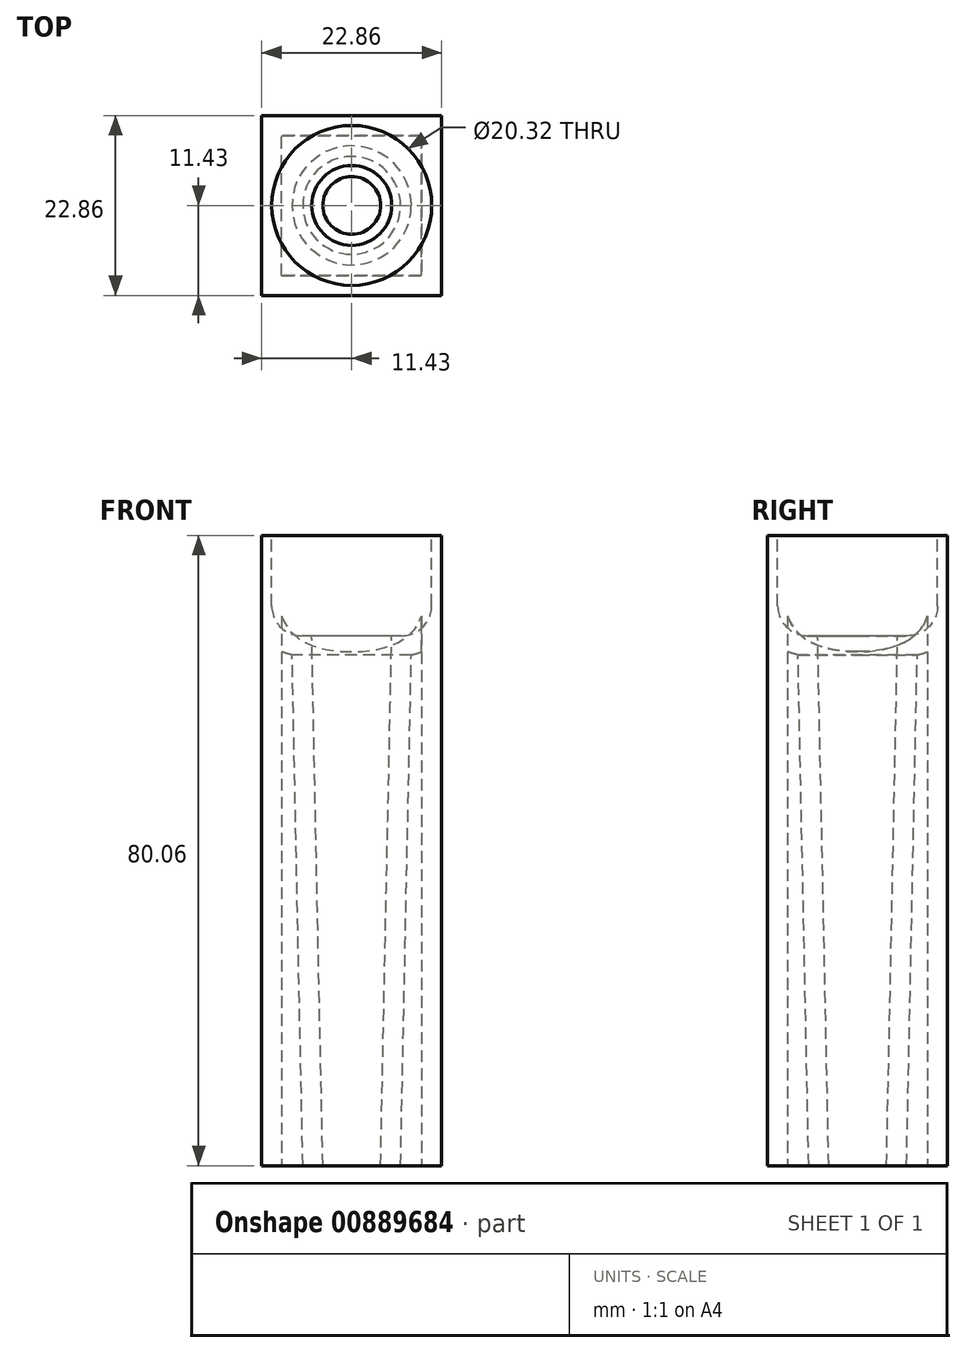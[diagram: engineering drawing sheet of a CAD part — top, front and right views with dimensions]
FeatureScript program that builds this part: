
annotation { "Feature Type Name" : "Feature", "Feature Type Description" : "" }
export const myFeature = defineFeature(function(context is Context, id is Id, definition is map)
    precondition{}
    {
        {
            var Q0;
            Q0=qCreatedBy(makeId("Top.planeOp"),FACE);
            var sketch = newSketch(context, id + "F0", { "sketchPlane" : qUnion([Q0])});
            skLineSegment(sketch, "E0.bottom", {"start": v(11.43, -11.43) * mm, "end": v(-11.43, -11.43) * mm});
            skLineSegment(sketch, "E0.top", {"start": v(11.43, 11.43) * mm, "end": v(-11.43, 11.43) * mm});
            skLineSegment(sketch, "E0.left", {"start": v(11.43, -11.43) * mm, "end": v(11.43, 11.43) * mm});
            skLineSegment(sketch, "E0.right", {"start": v(-11.43, -11.43) * mm, "end": v(-11.43, 11.43) * mm});
            skPoint(sketch, "E0.middle", {"position": v(0, 0) * mm});
            skSolve(sketch);
        }
        {
            var Q0;
            Q0 = qSketchRegion(id + "F0", true);
            extrude(context, id + "F1", {"entities" : qUnion([Q0]), "depth" : 67.3 * mm, "offsetDistance" : 25.4 * mm});
        }
        {
            var Q0;
            Q0=makeQuery(id+"F1.opExtrude","CAP_FACE",FACE,{"disambiguationData":[OSD([sQuery(id+"F0.wireOp",EDGE,"E0.bottom"),sQuery(id+"F0.wireOp",EDGE,"E0.top"),sQuery(id+"F0.wireOp",EDGE,"E0.left"),sQuery(id+"F0.wireOp",EDGE,"E0.right")])],"isStart":false});
            var sketch = newSketch(context, id + "F2", { "sketchPlane" : qUnion([Q0])});
            skLineSegment(sketch, "E1.bottom", {"start": v(11.43, -11.43) * mm, "end": v(-11.43, -11.43) * mm});
            skLineSegment(sketch, "E1.top", {"start": v(11.43, 11.43) * mm, "end": v(-11.43, 11.43) * mm});
            skLineSegment(sketch, "E1.left", {"start": v(11.43, -11.43) * mm, "end": v(11.43, 11.43) * mm});
            skLineSegment(sketch, "E1.right", {"start": v(-11.43, -11.43) * mm, "end": v(-11.43, 11.43) * mm});
            skPoint(sketch, "E1.middle", {"position": v(0, 0) * mm});
            skSolve(sketch);
        }
        {
            var Q0;
            Q0 = qSketchRegion(id + "F2", true);
            extrude(context, id + "F3", {"entities" : qUnion([Q0]), "operationType" : NewBodyOperationType.ADD, "depth" : 12.75 * mm, "offsetDistance" : 25.4 * mm});
        }
        {
            var Q0;
            Q0=qCreatedBy(makeId("Right.planeOp"),FACE);
            var sketch = newSketch(context, id + "F4", { "sketchPlane" : qUnion([Q0])});
            skLineSegment(sketch, "E2", {"start": v(0, 67.31) * mm, "end": v(-5.08, 67.31) * mm});
            skLineSegment(sketch, "E3", {"start": v(0, 67.31) * mm, "end": v(0, -11.43) * mm});
            skLineSegment(sketch, "E4", {"start": v(0, -11.43) * mm, "end": v(-3.43, -11.43) * mm});
            skLineSegment(sketch, "E5", {"start": v(-5.08, 67.31) * mm, "end": v(-3.43, -11.43) * mm});
            skSolve(sketch);
        }
        {
            var Q0;
            Q0=makeQuery(id+"F4.imprint","IMPRINT",FACE,{"disambiguationData":[TD([[makeQuery(id+"F4.imprint","IMPRINT",EDGE,{"derivedFrom":sQuery(id+"F4.wireOp",EDGE,"E2")}),1.0]])]});
            var Q1;
            Q1=sQuery(id+"F4.wireOp",EDGE,"E3");
            revolve(context, id + "F5", {"operationType" : NewBodyOperationType.REMOVE, "surfaceOperationType" : NewSurfaceOperationType.NEW, "entities" : qUnion([Q0]), "axis" : qUnion([Q1]), "revolveType" : RevolveType.FULL, "oppositeDirection" : true});
        }
        {
            var Q0;
            Q0=qCreatedBy(makeId("Right.planeOp"),FACE);
            var sketch = newSketch(context, id + "F6", { "sketchPlane" : qUnion([Q0])});
            skLineSegment(sketch, "E6", {"start": v(0, 67.31) * mm, "end": v(0, 83.82) * mm});
            skLineSegment(sketch, "E7", {"start": v(0, 83.82) * mm, "end": v(6.35, 83.82) * mm});
            skLineSegment(sketch, "E8", {"start": v(0, 67.31) * mm, "end": v(6.35, 67.31) * mm});
            skLineSegment(sketch, "E9", {"start": v(10.16, 80.01) * mm, "end": v(10.16, 71.12) * mm});
            skPoint(sketch, "E10.visualSharp", {"position": v(10.16, 83.82) * mm});
            skArc(sketch, "E10.filletArc", {"start": v(10.16, 80.01) * mm, "mid": v(9.04, 82.7) * mm, "end": v(6.35, 83.82) * mm});
            skPoint(sketch, "E11.visualSharp", {"position": v(10.16, 67.31) * mm});
            skArc(sketch, "E11.filletArc", {"start": v(6.35, 67.31) * mm, "mid": v(9.04, 68.43) * mm, "end": v(10.16, 71.12) * mm});
            skSolve(sketch);
        }
        {
            var Q0;
            Q0 = qSketchRegion(id + "F6", true);
            var Q1;
            Q1=sQuery(id+"F6.wireOp",EDGE,"E6");
            revolve(context, id + "F7", {"operationType" : NewBodyOperationType.REMOVE, "surfaceOperationType" : NewSurfaceOperationType.NEW, "entities" : qUnion([Q0]), "axis" : qUnion([Q1]), "revolveType" : RevolveType.FULL, "oppositeDirection" : true});
        }
        {
            var Q0;
            Q0=makeQuery(id+"F1.opExtrude","CAP_FACE",FACE,{"disambiguationData":[OSD([sQuery(id+"F0.wireOp",EDGE,"E0.bottom"),sQuery(id+"F0.wireOp",EDGE,"E0.top"),sQuery(id+"F0.wireOp",EDGE,"E0.left"),sQuery(id+"F0.wireOp",EDGE,"E0.right")])],"isStart":true});
            shell(context, id + "F8", {"entities" : qUnion([Q0]), "thickness" : 2.54 * mm});
        }
    });
